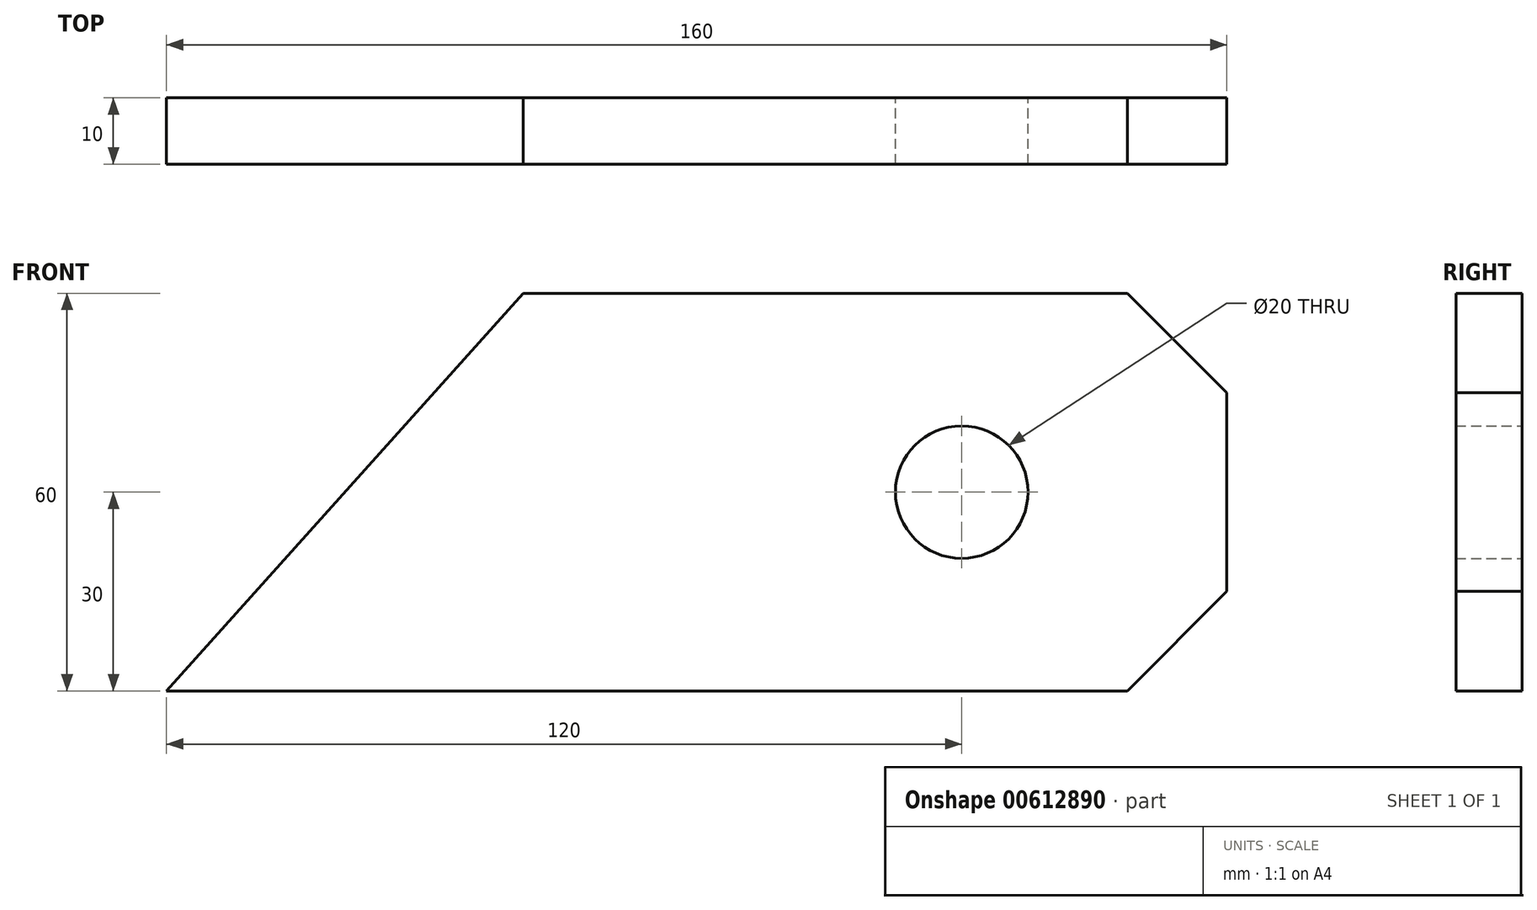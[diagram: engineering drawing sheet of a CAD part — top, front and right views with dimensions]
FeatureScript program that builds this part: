
annotation { "Feature Type Name" : "Feature", "Feature Type Description" : "" }
export const myFeature = defineFeature(function(context is Context, id is Id, definition is map)
    precondition{}
    {
        {
            var Q0;
            Q0=qCreatedBy(makeId("Front.planeOp"),FACE);
            var sketch = newSketch(context, id + "F0", { "sketchPlane" : qUnion([Q0])});
            skLineSegment(sketch, "E0.bottom", {"start": v(80, 30) * mm, "end": v(-80, 30) * mm});
            skLineSegment(sketch, "E0.top", {"start": v(80, -30) * mm, "end": v(-80, -30) * mm});
            skLineSegment(sketch, "E0.left", {"start": v(80, 30) * mm, "end": v(80, -30) * mm});
            skLineSegment(sketch, "E0.right", {"start": v(-80, 30) * mm, "end": v(-80, -30) * mm});
            skPoint(sketch, "E0.middle", {"position": v(0, 0) * mm});
            skCircle(sketch, "E1", {"center": v(40, 0) * mm, "radius": 10 * mm});
            skSolve(sketch);
        }
        {
            var Q0;
            Q0=makeQuery(id+"F0.imprint","IMPRINT",FACE,{"disambiguationData":[TD([[makeQuery(id+"F0.imprint","IMPRINT",EDGE,{"derivedFrom":sQuery(id+"F0.wireOp",EDGE,"E0.bottom")}),1.0]])]});
            extrude(context, id + "F1", {"entities" : qUnion([Q0]), "endBound" : BoundingType.SYMMETRIC, "depth" : 10 * mm, "offsetDistance" : 25 * mm});
        }
        {
            var Q0;
            Q0=makeQuery(id+"F1.opExtrude","SWEPT_EDGE",EDGE,{"disambiguationData":[OSD([sQuery(id+"F0.wireOp",EDGE,"E0.bottom"),sQuery(id+"F0.wireOp",EDGE,"E0.left")])]});
            var Q1;
            Q1=makeQuery(id+"F1.opExtrude","SWEPT_EDGE",EDGE,{"disambiguationData":[OSD([sQuery(id+"F0.wireOp",EDGE,"E0.top"),sQuery(id+"F0.wireOp",EDGE,"E0.left")])]});
            chamfer(context, id + "F2", {"entities" : qUnion([Q0, Q1]), "width" : 15 * mm, "tangentPropagation" : true});
        }
        {
            var Q0;
            Q0=makeQuery(id+"F1.opExtrude","CAP_FACE",FACE,{"disambiguationData":[OSD([sQuery(id+"F0.wireOp",EDGE,"E0.bottom"),sQuery(id+"F0.wireOp",EDGE,"E0.top"),sQuery(id+"F0.wireOp",EDGE,"E0.left"),sQuery(id+"F0.wireOp",EDGE,"E0.right"),sQuery(id+"F0.wireOp",EDGE,"E1")])],"isStart":false});
            var sketch = newSketch(context, id + "F3", { "sketchPlane" : qUnion([Q0])});
            skLineSegment(sketch, "E2", {"start": v(-80, -30) * mm, "end": v(-26.19, 30) * mm});
            skSolve(sketch);
        }
        {
            var Q0;
            {var subQ0=sQuery(id+"F3.wireOp",EDGE,"E2");Q0=makeQuery(id+"F3.imprint","IMPRINT",FACE,{"disambiguationData":[TD([[makeQuery(id+"F3.imprint","IMPRINT",EDGE,{"derivedFrom":subQ0}),1.0]])]});}
            extrude(context, id + "F4", {"entities" : qUnion([Q0]), "operationType" : NewBodyOperationType.REMOVE, "oppositeDirection" : true, "depth" : 25 * mm, "offsetDistance" : 25 * mm});
        }
    });
